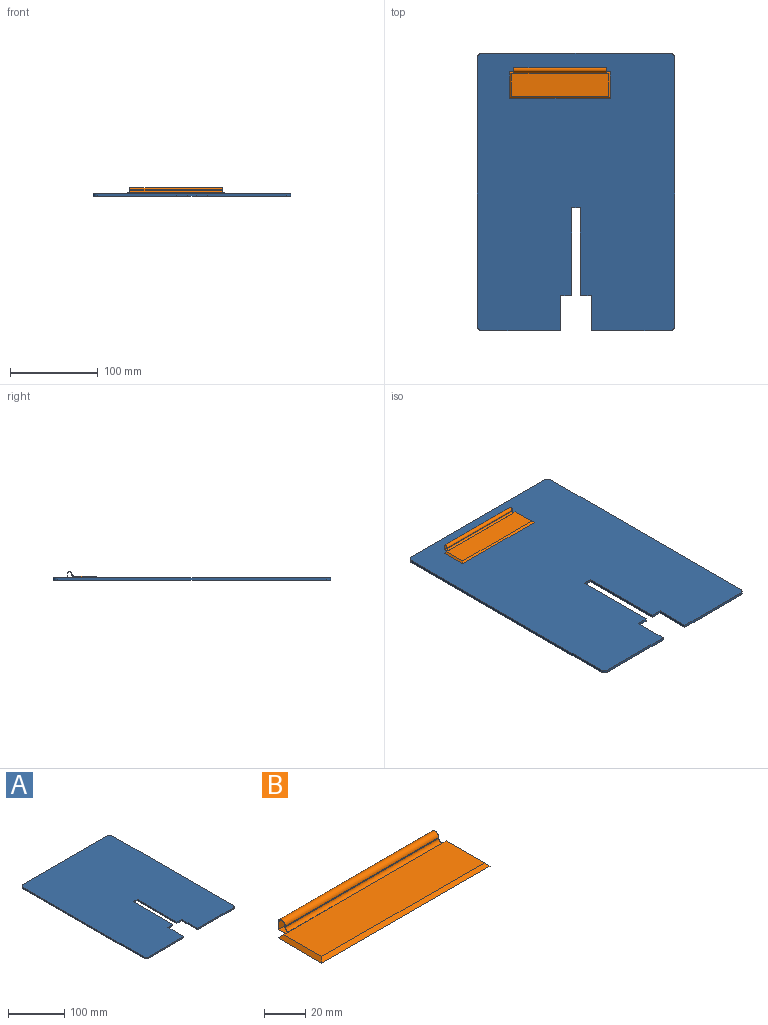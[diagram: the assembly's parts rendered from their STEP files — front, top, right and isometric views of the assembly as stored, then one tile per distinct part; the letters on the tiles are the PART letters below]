
ASSEMBLY  parts=2 mates=1
PART A: 18 faces, bbox 225x316x3 mm
  f0: plane 40x3mm, normal (-1,0,0), area 120mm2, adj f1,f6,f7,f8
  f1: plane 90x3mm, normal (0,-1,0), area 270mm2, adj f0,f7,f8,f9
  f2: plane 306x3mm, normal (1,0,0), area 918mm2, adj f7,f8,f9,f10
  f3: plane 215x3mm, normal (0,1,0), area 645mm2, adj f7,f8,f10,f17
  f4: plane 10x3mm, normal (0,-1,0), area 30mm2, adj f5,f7,f8,f14
  f5: plane 100x3mm, normal (-1,0,0), area 300mm2, adj f4,f6,f7,f8
  f6: plane 12.5x3mm, normal (0,-1,0), area 37.5mm2, adj f0,f5,f7,f8
  f7: plane 316x225mm, normal (0,0,1), area 68678.5mm2, adj f0,f1,f2,f3,f4,f5,f6,f9
  f8: plane 316x225mm, normal (0,0,-1), area 68678.5mm2, adj f0,f1,f2,f3,f4,f5,f6,f9
  f9: cylinder r=5mm len=5mm, axis (0,0,-1), area 23.6mm2, adj f1,f2,f7,f8
  f10: cylinder r=5mm len=5mm, axis (0,0,1), area 23.6mm2, adj f2,f3,f7,f8
  f11: plane 40x3mm, normal (1,0,0), area 120mm2, adj f7,f8,f12,f15
  f12: plane 90x3mm, normal (0,-1,0), area 270mm2, adj f7,f8,f11,f16
  f13: plane 306x3mm, normal (-1,0,0), area 918mm2, adj f7,f8,f16,f17
  f14: plane 100x3mm, normal (1,0,0), area 300mm2, adj f4,f7,f8,f15
  f15: plane 12.5x3mm, normal (0,-1,0), area 37.5mm2, adj f7,f8,f11,f14
  f16: cylinder r=5mm len=5mm, axis (0,0,-1), area 23.6mm2, adj f7,f8,f12,f13
  f17: cylinder r=5mm len=5mm, axis (0,0,1), area 23.6mm2, adj f3,f7,f8,f13
PART B: 16 faces, bbox 115x35x7 mm
  f0: plane 115x2mm, normal (0,0.71,0.71), area 250.9mm2, adj f2,f3,f4,f7,f11,f12,f14,f15
  f1: plane 115x2mm, normal (0,-0.71,0.71), area 319.6mm2, adj f2,f3,f4,f14
  f2: plane 115x35mm, normal (0,0,-1), area 3975mm2, adj f0,f1,f4,f6,f7,f14,f15
  f3: plane 111x26mm, normal (0,0,1), area 2886mm2, adj f0,f1,f4,f9,f14
  f4: plane 30x2mm, normal (0.71,0,0.71), area 79.2mm2, adj f0,f1,f2,f3
  f5: plane 105x0.5mm, normal (0,-1,0), area 52.5mm2, adj f7,f8,f9,f15
  f6: plane 105x4.5mm, normal (0,1,0), area 472.5mm2, adj f2,f7,f8,f15
  f7: plane 7x7mm, normal (1,0,0), area 5mm2, adj f0,f2,f5,f6,f8,f9,f10,f11
  f8: cylinder r=2.5mm len=105mm, axis (-1,0,0), area 824.7mm2, adj f5,f6,f7,f15
  f9: cylinder r=2mm len=105mm, axis (1,0,0), area 329.9mm2, adj f3,f5,f7,f15
  f10: cylinder r=2.25mm len=105mm, axis (1,0,0), area 768.3mm2, adj f7,f11,f13,f15
  f11: cylinder r=2.28mm len=105mm, axis (1,0,0), area 374.5mm2, adj f0,f7,f10,f15
  f12: plane 105x4.95mm, normal (0,0,1), area 519.8mm2, adj f0,f7,f13,f15
  f13: plane 105x4.3mm, normal (0,-1,0), area 451.5mm2, adj f7,f10,f12,f15
  f14: plane 30x2mm, normal (-0.71,0,0.71), area 79.2mm2, adj f0,f1,f2,f3
  f15: plane 7x7mm, normal (-1,0,0), area 5mm2, adj f0,f2,f5,f6,f8,f9,f10,f11
PLACE A t=(-52.17,-119.69,101.15)mm fixed
PLACE B rot(axis=(1,0,0),0deg) t=(-70.36,145.12,104.15)mm
MATE planar B.f2 <-> A.f7  axis (0,0,-1) through (-127.86,160.12,104.15)mm
